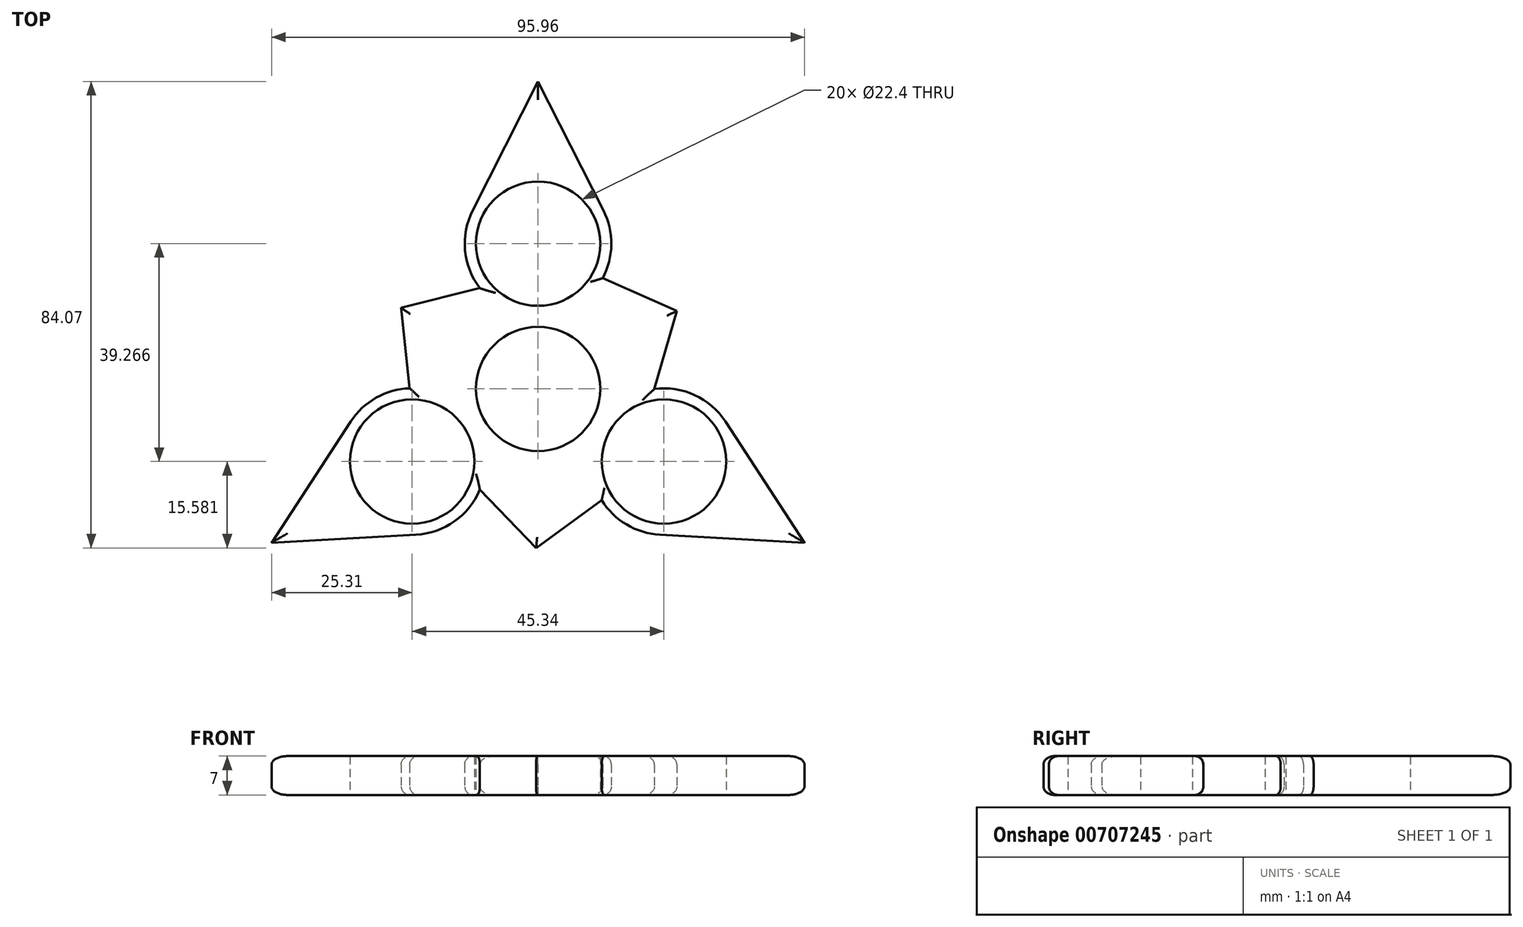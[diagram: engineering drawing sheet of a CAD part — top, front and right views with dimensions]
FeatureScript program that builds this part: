
annotation { "Feature Type Name" : "Feature", "Feature Type Description" : "" }
export const myFeature = defineFeature(function(context is Context, id is Id, definition is map)
    precondition{}
    {
        {
            var Q0;
            Q0=qCreatedBy(makeId("Top.planeOp"),FACE);
            var sketch = newSketch(context, id + "F0", { "sketchPlane" : qUnion([Q0])});
            skCircle(sketch, "E0", {"center": v(0, 0) * mm, "radius": 11.2 * mm});
            skCircle(sketch, "E1", {"center": v(0, 26.18) * mm, "radius": 11.2 * mm});
            skArc(sketch, "E2", {"start": v(11.65, 19.96) * mm, "mid": v(-1.08, 39.33) * mm, "end": v(-10.48, 18.15) * mm});
            skArc(sketch, "E3.1.0", {"start": v(-23.11, 0.1) * mm, "mid": v(-33.52, -20.6) * mm, "end": v(-10.48, -18.15) * mm});
            skCircle(sketch, "E3.1.1", {"center": v(-22.67, -13.09) * mm, "radius": 11.2 * mm});
            skArc(sketch, "E3.2.0", {"start": v(11.47, -20.07) * mm, "mid": v(34.6, -18.73) * mm, "end": v(20.96, 0) * mm});
            skCircle(sketch, "E3.2.1", {"center": v(22.67, -13.09) * mm, "radius": 11.2 * mm});
            skArc(sketch, "E4", {"start": v(11.65, 19.96) * mm, "mid": v(11.76, 7.86) * mm, "end": v(20.96, 0) * mm});
            skArc(sketch, "E5.1.0", {"start": v(-23.11, 0.1) * mm, "mid": v(-12.69, 6.25) * mm, "end": v(-10.48, 18.15) * mm});
            skArc(sketch, "E5.2.0", {"start": v(11.47, -20.07) * mm, "mid": v(0.93, -14.12) * mm, "end": v(-10.48, -18.15) * mm});
            skLineSegment(sketch, "E6", {"start": v(-11.77, 32.16) * mm, "end": v(0, 55.4) * mm});
            skLineSegment(sketch, "E7", {"start": v(0, 55.4) * mm, "end": v(11.78, 32.14) * mm});
            skLineSegment(sketch, "E8.1.0", {"start": v(-47.98, -27.7) * mm, "end": v(-33.72, -5.87) * mm});
            skLineSegment(sketch, "E8.1.1", {"start": v(-21.97, -26.27) * mm, "end": v(-47.98, -27.7) * mm});
            skLineSegment(sketch, "E8.2.0", {"start": v(47.98, -27.7) * mm, "end": v(21.95, -26.27) * mm});
            skLineSegment(sketch, "E8.2.1", {"start": v(33.74, -5.9) * mm, "end": v(47.98, -27.7) * mm});
            skLineSegment(sketch, "E9", {"start": v(-23.11, 0.1) * mm, "end": v(-24.65, 14.63) * mm});
            skLineSegment(sketch, "E10", {"start": v(-24.65, 14.63) * mm, "end": v(-10.48, 18.15) * mm});
            skLineSegment(sketch, "E11.1.0", {"start": v(-0.34, -28.67) * mm, "end": v(-10.48, -18.15) * mm});
            skLineSegment(sketch, "E11.1.1", {"start": v(11.47, -20.07) * mm, "end": v(-0.34, -28.67) * mm});
            skLineSegment(sketch, "E11.2.0", {"start": v(25, 14.04) * mm, "end": v(20.96, 0) * mm});
            skLineSegment(sketch, "E11.2.1", {"start": v(11.65, 19.96) * mm, "end": v(25, 14.04) * mm});
            skSolve(sketch);
        }
        {
            var Q0;
            Q0 = qSketchRegion(id + "F0", true);
            extrude(context, id + "F1", {"entities" : qUnion([Q0]), "depth" : 7 * mm, "offsetDistance" : 25 * mm});
        }
        {
            var Q0;
            Q0=makeQuery(id+"F1.opExtrude","CAP_EDGE",EDGE,{"disambiguationData":[OSD([sQuery(id+"F0.wireOp",EDGE,"E11.1.1")])],"isStart":false});
            var Q1;
            Q1=makeQuery(id+"F1.opExtrude","CAP_EDGE",EDGE,{"disambiguationData":[OSD([sQuery(id+"F0.wireOp",EDGE,"E11.1.0")])],"isStart":false});
            var Q2;
            {var subQ0=sQuery(id+"F0.wireOp",EDGE,"E3.1.0");Q2=makeQuery(id+"F1.opExtrude","CAP_EDGE",EDGE,{"disambiguationData":[OSD([subQ0]),TDD([makeQuery(id+"F0.imprint","IMPRINT",EDGE,{"disambiguationData":[TD([[makeQuery(id+"F0.imprint","INTERSECT",VERTEX,{"derivedFrom":[subQ0,sQuery(id+"F0.wireOp",EDGE,"E8.1.1")]}),-1.0]])],"derivedFrom":subQ0})])],"isStart":false});}
            var Q3;
            Q3=makeQuery(id+"F1.opExtrude","CAP_EDGE",EDGE,{"disambiguationData":[OSD([sQuery(id+"F0.wireOp",EDGE,"E8.1.1")])],"isStart":false});
            var Q4;
            Q4=makeQuery(id+"F1.opExtrude","CAP_EDGE",EDGE,{"disambiguationData":[OSD([sQuery(id+"F0.wireOp",EDGE,"E8.1.0")])],"isStart":false});
            var Q5;
            {var subQ0=sQuery(id+"F0.wireOp",EDGE,"E3.1.0");Q5=makeQuery(id+"F1.opExtrude","CAP_EDGE",EDGE,{"disambiguationData":[OSD([subQ0]),TDD([makeQuery(id+"F0.imprint","IMPRINT",EDGE,{"disambiguationData":[TD([[makeQuery(id+"F0.imprint","INTERSECT",VERTEX,{"derivedFrom":[subQ0,sQuery(id+"F0.wireOp",EDGE,"E8.1.0")]}),1.0]])],"derivedFrom":subQ0})])],"isStart":false});}
            var Q6;
            Q6=makeQuery(id+"F1.opExtrude","CAP_EDGE",EDGE,{"disambiguationData":[OSD([sQuery(id+"F0.wireOp",EDGE,"E9")])],"isStart":false});
            var Q7;
            Q7=makeQuery(id+"F1.opExtrude","CAP_EDGE",EDGE,{"disambiguationData":[OSD([sQuery(id+"F0.wireOp",EDGE,"E10")])],"isStart":false});
            var Q8;
            {var subQ0=sQuery(id+"F0.wireOp",EDGE,"E2");Q8=makeQuery(id+"F1.opExtrude","CAP_EDGE",EDGE,{"disambiguationData":[OSD([subQ0]),TDD([makeQuery(id+"F0.imprint","IMPRINT",EDGE,{"disambiguationData":[TD([[makeQuery(id+"F0.imprint","INTERSECT",VERTEX,{"derivedFrom":[subQ0,sQuery(id+"F0.wireOp",EDGE,"E6")]}),-1.0]])],"derivedFrom":subQ0})])],"isStart":false});}
            var Q9;
            Q9=makeQuery(id+"F1.opExtrude","CAP_EDGE",EDGE,{"disambiguationData":[OSD([sQuery(id+"F0.wireOp",EDGE,"E6")])],"isStart":false});
            var Q10;
            {var subQ0=sQuery(id+"F0.wireOp",EDGE,"E3.2.0");Q10=makeQuery(id+"F1.opExtrude","CAP_EDGE",EDGE,{"disambiguationData":[OSD([subQ0]),TDD([makeQuery(id+"F0.imprint","IMPRINT",EDGE,{"disambiguationData":[TD([[makeQuery(id+"F0.imprint","INTERSECT",VERTEX,{"derivedFrom":[subQ0,sQuery(id+"F0.wireOp",EDGE,"E8.2.0")]}),1.0]])],"derivedFrom":subQ0})])],"isStart":false});}
            var Q11;
            Q11=makeQuery(id+"F1.opExtrude","CAP_EDGE",EDGE,{"disambiguationData":[OSD([sQuery(id+"F0.wireOp",EDGE,"E8.2.0")])],"isStart":false});
            var Q12;
            Q12=makeQuery(id+"F1.opExtrude","CAP_EDGE",EDGE,{"disambiguationData":[OSD([sQuery(id+"F0.wireOp",EDGE,"E8.2.1")])],"isStart":false});
            var Q13;
            {var subQ0=sQuery(id+"F0.wireOp",EDGE,"E3.2.0");Q13=makeQuery(id+"F1.opExtrude","CAP_EDGE",EDGE,{"disambiguationData":[OSD([subQ0]),TDD([makeQuery(id+"F0.imprint","IMPRINT",EDGE,{"disambiguationData":[TD([[makeQuery(id+"F0.imprint","INTERSECT",VERTEX,{"derivedFrom":[subQ0,sQuery(id+"F0.wireOp",EDGE,"E8.2.1")]}),-1.0]])],"derivedFrom":subQ0})])],"isStart":false});}
            var Q14;
            Q14=makeQuery(id+"F1.opExtrude","CAP_EDGE",EDGE,{"disambiguationData":[OSD([sQuery(id+"F0.wireOp",EDGE,"E11.2.0")])],"isStart":false});
            var Q15;
            Q15=makeQuery(id+"F1.opExtrude","CAP_EDGE",EDGE,{"disambiguationData":[OSD([sQuery(id+"F0.wireOp",EDGE,"E11.2.1")])],"isStart":false});
            var Q16;
            {var subQ0=sQuery(id+"F0.wireOp",EDGE,"E2");Q16=makeQuery(id+"F1.opExtrude","CAP_EDGE",EDGE,{"disambiguationData":[OSD([subQ0]),TDD([makeQuery(id+"F0.imprint","IMPRINT",EDGE,{"disambiguationData":[TD([[makeQuery(id+"F0.imprint","INTERSECT",VERTEX,{"derivedFrom":[subQ0,sQuery(id+"F0.wireOp",EDGE,"E7")]}),1.0]])],"derivedFrom":subQ0})])],"isStart":false});}
            var Q17;
            Q17=makeQuery(id+"F1.opExtrude","CAP_EDGE",EDGE,{"disambiguationData":[OSD([sQuery(id+"F0.wireOp",EDGE,"E7")])],"isStart":true});
            var Q18;
            Q18=makeQuery(id+"F1.opExtrude","CAP_EDGE",EDGE,{"disambiguationData":[OSD([sQuery(id+"F0.wireOp",EDGE,"E8.1.0")])],"isStart":true});
            var Q19;
            {var subQ0=sQuery(id+"F0.wireOp",EDGE,"E3.1.0");Q19=makeQuery(id+"F1.opExtrude","CAP_EDGE",EDGE,{"disambiguationData":[OSD([subQ0]),TDD([makeQuery(id+"F0.imprint","IMPRINT",EDGE,{"disambiguationData":[TD([[makeQuery(id+"F0.imprint","INTERSECT",VERTEX,{"derivedFrom":[subQ0,sQuery(id+"F0.wireOp",EDGE,"E8.1.0")]}),1.0]])],"derivedFrom":subQ0})])],"isStart":true});}
            var Q20;
            Q20=makeQuery(id+"F1.opExtrude","CAP_EDGE",EDGE,{"disambiguationData":[OSD([sQuery(id+"F0.wireOp",EDGE,"E9")])],"isStart":true});
            var Q21;
            Q21=makeQuery(id+"F1.opExtrude","CAP_EDGE",EDGE,{"disambiguationData":[OSD([sQuery(id+"F0.wireOp",EDGE,"E10")])],"isStart":true});
            var Q22;
            {var subQ0=sQuery(id+"F0.wireOp",EDGE,"E2");Q22=makeQuery(id+"F1.opExtrude","CAP_EDGE",EDGE,{"disambiguationData":[OSD([subQ0]),TDD([makeQuery(id+"F0.imprint","IMPRINT",EDGE,{"disambiguationData":[TD([[makeQuery(id+"F0.imprint","INTERSECT",VERTEX,{"derivedFrom":[subQ0,sQuery(id+"F0.wireOp",EDGE,"E6")]}),-1.0]])],"derivedFrom":subQ0})])],"isStart":true});}
            var Q23;
            Q23=makeQuery(id+"F1.opExtrude","CAP_EDGE",EDGE,{"disambiguationData":[OSD([sQuery(id+"F0.wireOp",EDGE,"E6")])],"isStart":true});
            var Q24;
            Q24=makeQuery(id+"F1.opExtrude","CAP_EDGE",EDGE,{"disambiguationData":[OSD([sQuery(id+"F0.wireOp",EDGE,"E8.1.1")])],"isStart":true});
            var Q25;
            {var subQ0=sQuery(id+"F0.wireOp",EDGE,"E3.1.0");Q25=makeQuery(id+"F1.opExtrude","CAP_EDGE",EDGE,{"disambiguationData":[OSD([subQ0]),TDD([makeQuery(id+"F0.imprint","IMPRINT",EDGE,{"disambiguationData":[TD([[makeQuery(id+"F0.imprint","INTERSECT",VERTEX,{"derivedFrom":[subQ0,sQuery(id+"F0.wireOp",EDGE,"E8.1.1")]}),-1.0]])],"derivedFrom":subQ0})])],"isStart":true});}
            var Q26;
            Q26=makeQuery(id+"F1.opExtrude","CAP_EDGE",EDGE,{"disambiguationData":[OSD([sQuery(id+"F0.wireOp",EDGE,"E11.1.1")])],"isStart":true});
            var Q27;
            Q27=makeQuery(id+"F1.opExtrude","CAP_EDGE",EDGE,{"disambiguationData":[OSD([sQuery(id+"F0.wireOp",EDGE,"E11.2.0")])],"isStart":true});
            var Q28;
            Q28=makeQuery(id+"F1.opExtrude","CAP_EDGE",EDGE,{"disambiguationData":[OSD([sQuery(id+"F0.wireOp",EDGE,"E8.2.1")])],"isStart":true});
            var Q29;
            {var subQ0=sQuery(id+"F0.wireOp",EDGE,"E2");Q29=makeQuery(id+"F1.opExtrude","CAP_EDGE",EDGE,{"disambiguationData":[OSD([subQ0]),TDD([makeQuery(id+"F0.imprint","IMPRINT",EDGE,{"disambiguationData":[TD([[makeQuery(id+"F0.imprint","INTERSECT",VERTEX,{"derivedFrom":[subQ0,sQuery(id+"F0.wireOp",EDGE,"E7")]}),1.0]])],"derivedFrom":subQ0})])],"isStart":true});}
            var Q30;
            {var subQ0=sQuery(id+"F0.wireOp",EDGE,"E3.2.0");Q30=makeQuery(id+"F1.opExtrude","CAP_EDGE",EDGE,{"disambiguationData":[OSD([subQ0]),TDD([makeQuery(id+"F0.imprint","IMPRINT",EDGE,{"disambiguationData":[TD([[makeQuery(id+"F0.imprint","INTERSECT",VERTEX,{"derivedFrom":[subQ0,sQuery(id+"F0.wireOp",EDGE,"E8.2.1")]}),-1.0]])],"derivedFrom":subQ0})])],"isStart":true});}
            var Q31;
            Q31=makeQuery(id+"F1.opExtrude","CAP_EDGE",EDGE,{"disambiguationData":[OSD([sQuery(id+"F0.wireOp",EDGE,"E8.2.0")])],"isStart":true});
            var Q32;
            Q32=makeQuery(id+"F1.opExtrude","CAP_EDGE",EDGE,{"disambiguationData":[OSD([sQuery(id+"F0.wireOp",EDGE,"E11.2.1")])],"isStart":true});
            var Q33;
            Q33=makeQuery(id+"F1.opExtrude","CAP_EDGE",EDGE,{"disambiguationData":[OSD([sQuery(id+"F0.wireOp",EDGE,"E11.1.0")])],"isStart":true});
            fillet(context, id + "F2", {"entities" : qUnion([Q0, Q1, Q2, Q3, Q4, Q5, Q6, Q7, Q8, Q9, Q10, Q11, Q12, Q13, Q14, Q15, Q16, Q17, Q18, Q19, Q20, Q21, Q22, Q23, Q24, Q25, Q26, Q27, Q28, Q29, Q30, Q31, Q32, Q33]), "radius" : 1.5 * mm, "tangentPropagation" : true, "allowEdgeOverflow" : false});
        }
    });
